# Revit family: 841 and 842 series
name_source: partatom
category: Mechanical Equipment
revit_build: Autodesk Revit 2013 (Build: 20120221_2030(x64)
units: mm (PartAtom-declared; Revit-internal decimal feet)

## types (12) — shared parameters
Assembly Code = D2010900
Cord Length = 240"
Default Elevation = 0"
Description = Commercial Effluent Pumps
Discharge Diameter = 1 1/4" NPT
Discharge Radius = 5/8"
Height = 20 5/8"
Hertz = 60
Impeller Type = Bronze Vortex
Installation Type = Floor Mounted
Length = 11 11/16"
Manufacturer = Zoeller
Masterformat Number = 33 36 16
Masterformat Title = Utility Septic Tank Effluent Pumps
Material = Cast Iron-Zoeller-Powder Coated Epoxy
Maximum Head = 1500"
Mechanical Seals = Dual with leak detection
Motor = 2 HP
Motor Thermal Shutoff = Thermal Overload (1 Ph), Thermal Sensor (3 Ph)
Motor Type = Submersible
Nominal Height = 5"
Omniclass Table 23 Code = 23.60.30.21
Omniclass Table 23 Title = Pumps
Operation = Non-Automatic
Overall Height = 23 3/4"
Price = Prices may vary. Please consult Manufacturer Representative for most up-to-date price list.
Product Page URL = http://www.zoellerpumps.com
RPM = 3450
Shipping Weight = 135 lbs.
Warranty Information = 36 Months (Limited)
Waste Connection = Yes
Width = 8 1/8"

## per-type parameters (varying)
| type | Amps | Apparent Load | Flow @ 5' | Impeller Diameter | Model | Phase | Type | URL | Voltage |
| 841-200V 1Ph | 20 A | 4000 VA | 61 GPM | 6 1/8" | 841 | 1 | Capacitor start/Capacitor Run | http://www.zoellerpumps.com | 200 V |
| 841-230V 1Ph | 17 A | 3956 VA | 61 GPM | 6 1/8" | 841 | 1 | Capacitor start/Capacitor Run | http://www.zoellerpumps.com | 230 V |
| 841-200V 3Ph | 12 A | 2460 VA | 61 GPM | 6 1/8" | 841 | 3 | 3Ph | http://www.zoellerpumps.com | 200 V |
| 841-230V 3Ph | 11 A | 2484 VA | 61 GPM | 6 1/8" | 841 | 3 | 3Ph | http://www.zoellerpumps.com | 230 V |
| 841-460V 3Ph | 6 A | 2530 VA | 61 GPM | 6 1/8" | 841 | 3 | 3Ph | http://www.zoellerpumps.com | 460 V |
| 841-575V 3Ph | 5 A | 2588 VA | 61 GPM | 6 1/8" | 841 | 3 | 3Ph | http://www.zoellerpumps.com | 575 V |
| 842-200V 1Ph | 20 A | 4000 VA | 34 GPM | 6 3/16" | 842 | 1 | Capacitor start/Capacitor Run | http://www.zoellerpumps.com | 200 V |
| 842-230V 1Ph | 17 A | 3956 VA | 34 GPM | 6 3/16" | 842 | 1 | Capacitor start/Capacitor Run | http://www.zoellerpumps.com | 230 V |
| 842-200V 3Ph | 12 A | 2460 VA | 34 GPM | 6 3/16" | 842 | 3 | 3Ph | http://www.zoellerpumpsd.com | 200 V |
| 842-230V 3Ph | 11 A | 2484 VA | 34 GPM | 6 3/16" | 842 | 3 | 3Ph | http://www.zoellerpumpsd.com | 230 V |
| 842-460V 3Ph | 6 A | 2530 VA | 34 GPM | 6 3/16" | 842 | 3 | 3Ph | http://www.zoellerpumpsd.com | 460 V |
| 842-575V 3Ph | 5 A | 2588 VA | 34 GPM | 6 3/16" | 842 | 3 | 3Ph | http://www.zoellerpumpsd.com | 575 V |

## geometry (parser evidence)
native form markers: Blend x6, Sweep x3
no freeform markers — native parametric forms only
